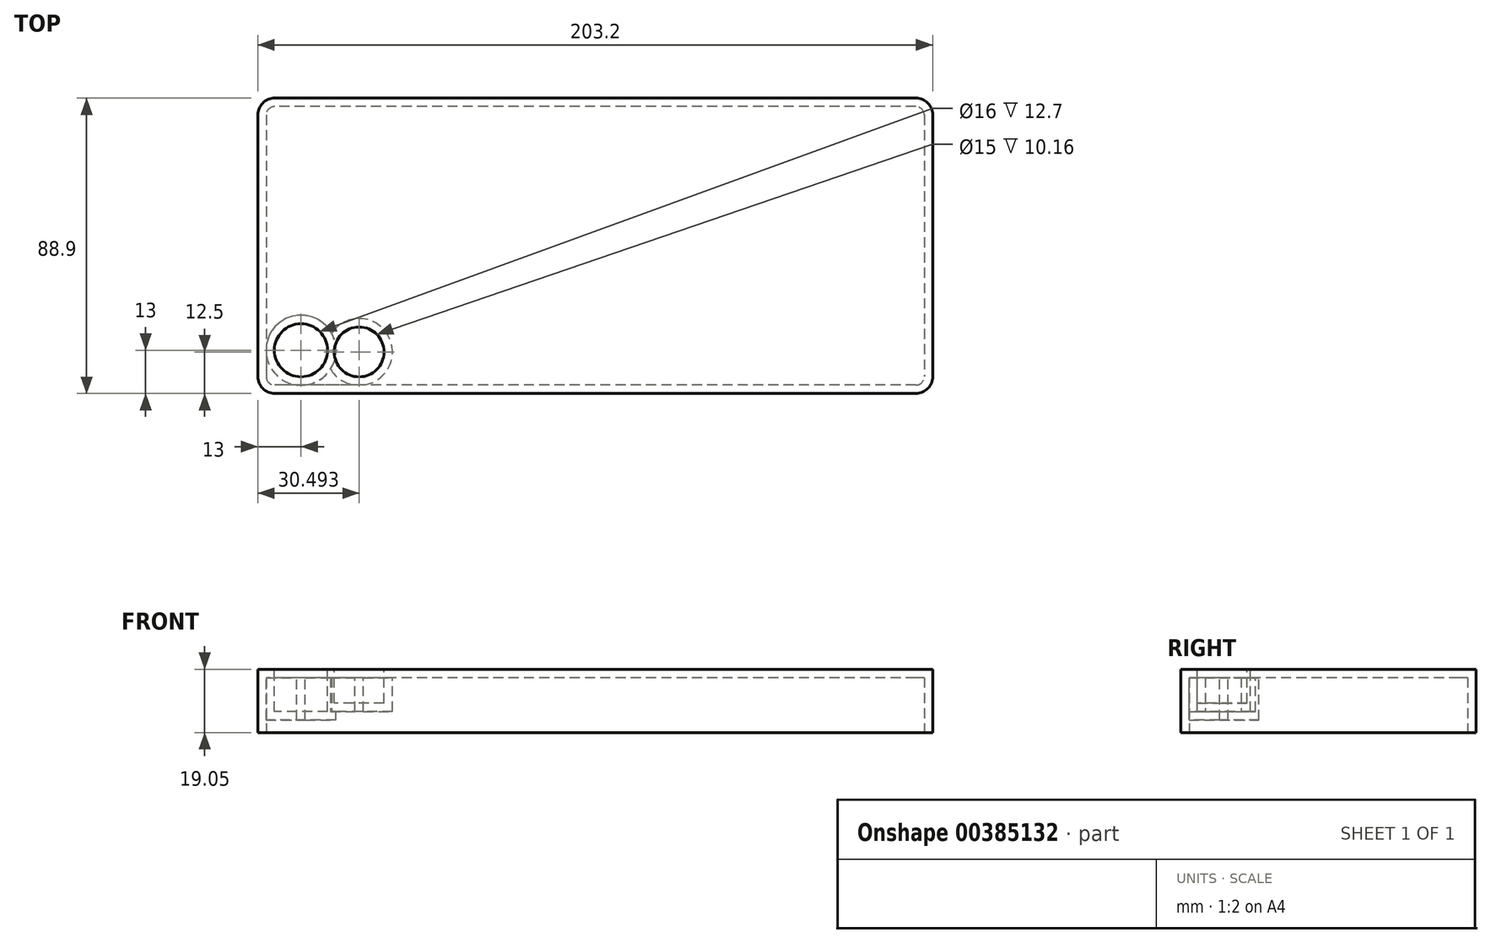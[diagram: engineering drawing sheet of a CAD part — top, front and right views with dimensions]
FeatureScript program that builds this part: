
annotation { "Feature Type Name" : "Feature", "Feature Type Description" : "" }
export const myFeature = defineFeature(function(context is Context, id is Id, definition is map)
    precondition{}
    {
        {
            var Q0;
            Q0=qCreatedBy(makeId("Top.planeOp"),FACE);
            var sketch = newSketch(context, id + "F0", { "sketchPlane" : qUnion([Q0])});
            skLineSegment(sketch, "E0.bottom", {"start": v(101.6, 44.45) * mm, "end": v(-101.6, 44.45) * mm});
            skLineSegment(sketch, "E0.top", {"start": v(101.6, -44.45) * mm, "end": v(-101.6, -44.45) * mm});
            skLineSegment(sketch, "E0.left", {"start": v(101.6, 44.45) * mm, "end": v(101.6, -44.45) * mm});
            skLineSegment(sketch, "E0.right", {"start": v(-101.6, 44.45) * mm, "end": v(-101.6, -44.45) * mm});
            skPoint(sketch, "E0.middle", {"position": v(0, 0) * mm});
            skSolve(sketch);
        }
        {
            var Q0;
            Q0 = qSketchRegion(id + "F0", true);
            extrude(context, id + "F1", {"entities" : qUnion([Q0]), "depth" : 19.05 * mm});
        }
        {
            var Q0;
            Q0=makeQuery(id+"F1.opExtrude","CAP_FACE",FACE,{"disambiguationData":[OSD([sQuery(id+"F0.wireOp",EDGE,"E0.bottom"),sQuery(id+"F0.wireOp",EDGE,"E0.top"),sQuery(id+"F0.wireOp",EDGE,"E0.left"),sQuery(id+"F0.wireOp",EDGE,"E0.right")])],"isStart":false});
            var sketch = newSketch(context, id + "F2", { "sketchPlane" : qUnion([Q0])});
            skLineSegment(sketch, "E1", {"start": v(-101.6, -39.45) * mm, "end": v(101.6, -39.45) * mm});
            skCircle(sketch, "E2", {"center": v(-88.6, -31.45) * mm, "radius": 8 * mm});
            skCircle(sketch, "E3", {"center": v(-71.1, -31.95) * mm, "radius": 7.5 * mm});
            skCircle(sketch, "E4", {"center": v(-54.61, -32.45) * mm, "radius": 7 * mm});
            skCircle(sketch, "E5", {"center": v(-39.12, -32.95) * mm, "radius": 6.5 * mm});
            skCircle(sketch, "E6", {"center": v(-24.63, -33.45) * mm, "radius": 6 * mm});
            skCircle(sketch, "E7", {"center": v(-11.14, -33.95) * mm, "radius": 5.5 * mm});
            skCircle(sketch, "E8", {"center": v(1.35, -34.45) * mm, "radius": 5 * mm});
            skCircle(sketch, "E9", {"center": v(13.35, -34.45) * mm, "radius": 5 * mm});
            skCircle(sketch, "E10", {"center": v(25.35, -34.45) * mm, "radius": 5 * mm});
            skCircle(sketch, "E11", {"center": v(37.35, -34.45) * mm, "radius": 5 * mm});
            skSolve(sketch);
        }
        {
            var Q0;
            Q0=makeQuery(id+"F2.imprint","IMPRINT",FACE,{"disambiguationData":[TD([[makeQuery(id+"F2.imprint","IMPRINT",EDGE,{"derivedFrom":sQuery(id+"F2.wireOp",EDGE,"E2")}),1.0]])]});
            var Q1;
            Q1=sQuery(id+"F2.wireOp",EDGE,"E2");
            extrude(context, id + "F3", {"entities" : qUnion([Q0]), "operationType" : NewBodyOperationType.REMOVE, "surfaceEntities" : qUnion([Q1]), "oppositeDirection" : true, "depth" : 12.7 * mm});
        }
        {
            var Q0;
            Q0=makeQuery(id+"F1.opExtrude","SWEPT_EDGE",EDGE,{"disambiguationData":[OSD([sQuery(id+"F0.wireOp",EDGE,"E0.top"),sQuery(id+"F0.wireOp",EDGE,"E0.right")])]});
            var Q1;
            Q1=makeQuery(id+"F1.opExtrude","SWEPT_EDGE",EDGE,{"disambiguationData":[OSD([sQuery(id+"F0.wireOp",EDGE,"E0.top"),sQuery(id+"F0.wireOp",EDGE,"E0.left")])]});
            var Q2;
            Q2=makeQuery(id+"F1.opExtrude","SWEPT_EDGE",EDGE,{"disambiguationData":[OSD([sQuery(id+"F0.wireOp",EDGE,"E0.bottom"),sQuery(id+"F0.wireOp",EDGE,"E0.left")])]});
            var Q3;
            Q3=makeQuery(id+"F1.opExtrude","SWEPT_EDGE",EDGE,{"disambiguationData":[OSD([sQuery(id+"F0.wireOp",EDGE,"E0.bottom"),sQuery(id+"F0.wireOp",EDGE,"E0.right")])]});
            fillet(context, id + "F4", {"entities" : qUnion([Q0, Q1, Q2, Q3]), "radius" : 5.08 * mm, "tangentPropagation" : true, "allowEdgeOverflow" : false});
        }
        {
            var Q0;
            Q0=makeQuery(id+"F2.imprint","IMPRINT",FACE,{"disambiguationData":[TD([[makeQuery(id+"F2.imprint","IMPRINT",EDGE,{"derivedFrom":sQuery(id+"F2.wireOp",EDGE,"E3")}),1.0]])]});
            var Q1;
            Q1=sQuery(id+"F2.wireOp",EDGE,"E3");
            extrude(context, id + "F5", {"entities" : qUnion([Q0]), "operationType" : NewBodyOperationType.REMOVE, "surfaceEntities" : qUnion([Q1]), "oppositeDirection" : true, "depth" : 10.16 * mm});
        }
        {
            var Q0;
            Q0=makeQuery(id+"F1.opExtrude","CAP_FACE",FACE,{"disambiguationData":[OSD([sQuery(id+"F0.wireOp",EDGE,"E0.bottom"),sQuery(id+"F0.wireOp",EDGE,"E0.top"),sQuery(id+"F0.wireOp",EDGE,"E0.left"),sQuery(id+"F0.wireOp",EDGE,"E0.right")])],"isStart":true});
            shell(context, id + "F6", {"entities" : qUnion([Q0]), "thickness" : 2.54 * mm});
        }
    });
